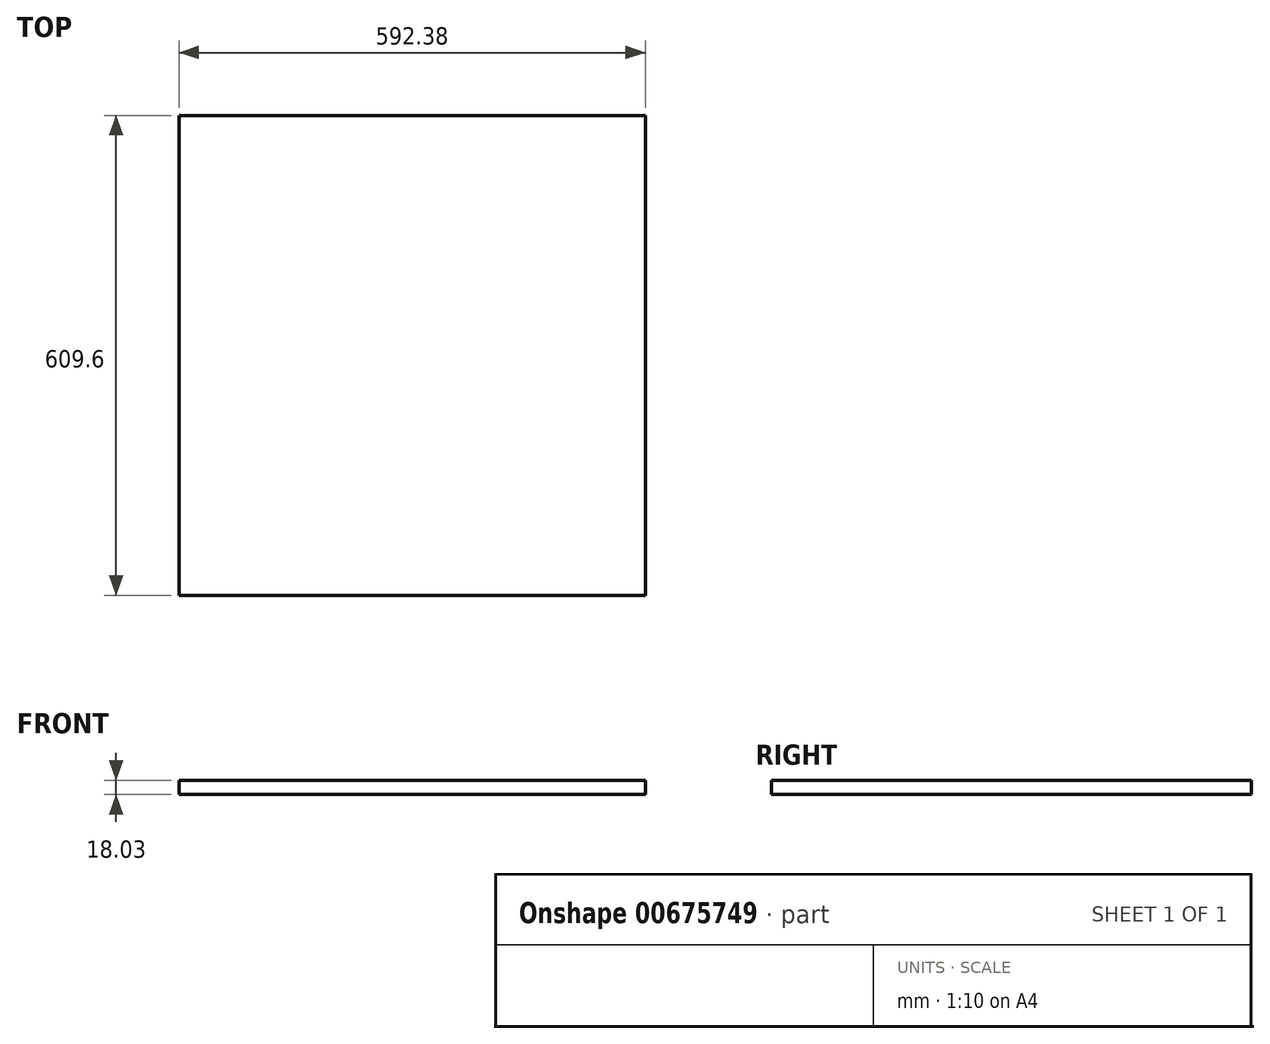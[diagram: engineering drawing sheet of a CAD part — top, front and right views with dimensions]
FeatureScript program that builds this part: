
annotation { "Feature Type Name" : "Feature", "Feature Type Description" : "" }
export const myFeature = defineFeature(function(context is Context, id is Id, definition is map)
    precondition{}
    {
        {
            var Q0;
            Q0=qCreatedBy(makeId("Top.planeOp"),FACE);
            var sketch = newSketch(context, id + "F0", { "sketchPlane" : qUnion([Q0])});
            skLineSegment(sketch, "E0.bottom", {"start": v(0, 0) * mm, "end": v(592.38, 0) * mm});
            skLineSegment(sketch, "E0.top", {"start": v(0, 609.6) * mm, "end": v(592.38, 609.6) * mm});
            skLineSegment(sketch, "E0.left", {"start": v(0, 0) * mm, "end": v(0, 609.6) * mm});
            skLineSegment(sketch, "E0.right", {"start": v(592.38, 0) * mm, "end": v(592.38, 609.6) * mm});
            skSolve(sketch);
        }
        {
            var Q0;
            Q0=qSketchRegion(id+"F0",true);
            extrude(context, id + "F1", {"entities" : qUnion([Q0]), "depth" : 18.03 * mm, "offsetDistance" : 25.4 * mm});
        }
    });
